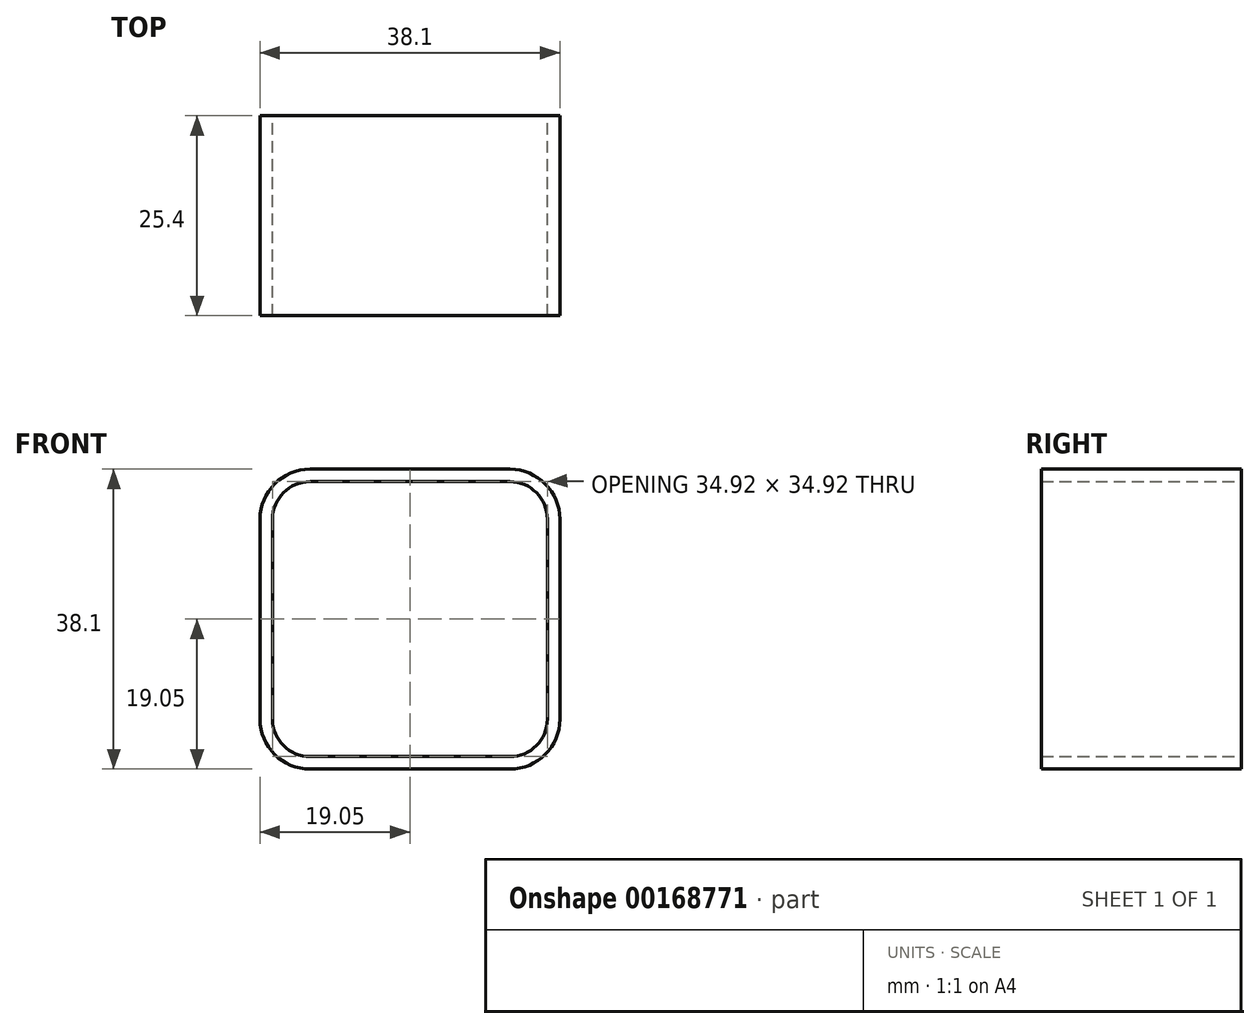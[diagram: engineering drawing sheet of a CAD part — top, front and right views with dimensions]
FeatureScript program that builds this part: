
annotation { "Feature Type Name" : "Feature", "Feature Type Description" : "" }
export const myFeature = defineFeature(function(context is Context, id is Id, definition is map)
    precondition{}
    {
        {
            var Q0;
            Q0=qCreatedBy(makeId("Front.planeOp"),FACE);
            var sketch = newSketch(context, id + "F0", { "sketchPlane" : qUnion([Q0])});
            skLineSegment(sketch, "E0.bottom", {"start": v(12.7, -19.05) * mm, "end": v(-12.7, -19.05) * mm});
            skLineSegment(sketch, "E0.top", {"start": v(12.7, 19.05) * mm, "end": v(-12.7, 19.05) * mm});
            skLineSegment(sketch, "E0.left", {"start": v(19.05, -12.7) * mm, "end": v(19.05, 12.7) * mm});
            skLineSegment(sketch, "E0.right", {"start": v(-19.05, -12.7) * mm, "end": v(-19.05, 12.7) * mm});
            skPoint(sketch, "E0.middle", {"position": v(0, 0) * mm});
            skPoint(sketch, "E1.visualSharp", {"position": v(-19.05, 19.05) * mm});
            skArc(sketch, "E1.filletArc", {"start": v(-12.7, 19.05) * mm, "mid": v(-17.2, 17.2) * mm, "end": v(-19.05, 12.7) * mm});
            skPoint(sketch, "E2.visualSharp", {"position": v(19.05, 19.05) * mm});
            skArc(sketch, "E2.filletArc", {"start": v(19.05, 12.7) * mm, "mid": v(17.2, 17.2) * mm, "end": v(12.7, 19.05) * mm});
            skPoint(sketch, "E3.visualSharp", {"position": v(19.05, -19.05) * mm});
            skArc(sketch, "E3.filletArc", {"start": v(12.7, -19.05) * mm, "mid": v(17.2, -17.2) * mm, "end": v(19.05, -12.7) * mm});
            skPoint(sketch, "E4.visualSharp", {"position": v(-19.05, -19.05) * mm});
            skArc(sketch, "E4.filletArc", {"start": v(-19.05, -12.7) * mm, "mid": v(-17.2, -17.2) * mm, "end": v(-12.7, -19.05) * mm});
            skLineSegment(sketch, "E5.0", {"start": v(12.7, 17.46) * mm, "end": v(-12.7, 17.46) * mm});
            skArc(sketch, "E5.1", {"start": v(17.46, 12.7) * mm, "mid": v(16.07, 16.07) * mm, "end": v(12.7, 17.46) * mm});
            skArc(sketch, "E5.2", {"start": v(-12.7, 17.46) * mm, "mid": v(-16.07, 16.07) * mm, "end": v(-17.46, 12.7) * mm});
            skLineSegment(sketch, "E5.3", {"start": v(17.46, -12.7) * mm, "end": v(17.46, 12.7) * mm});
            skLineSegment(sketch, "E5.4", {"start": v(-17.46, -12.7) * mm, "end": v(-17.46, 12.7) * mm});
            skArc(sketch, "E5.5", {"start": v(-17.46, -12.7) * mm, "mid": v(-16.07, -16.07) * mm, "end": v(-12.7, -17.46) * mm});
            skLineSegment(sketch, "E5.6", {"start": v(12.7, -17.46) * mm, "end": v(-12.7, -17.46) * mm});
            skArc(sketch, "E5.7", {"start": v(12.7, -17.46) * mm, "mid": v(16.07, -16.07) * mm, "end": v(17.46, -12.7) * mm});
            skSolve(sketch);
        }
        {
            var Q0;
            Q0=makeQuery(id+"F0.imprint","IMPRINT",FACE,{"disambiguationData":[TD([[makeQuery(id+"F0.imprint","IMPRINT",EDGE,{"derivedFrom":sQuery(id+"F0.wireOp",EDGE,"E0.bottom")}),-1.0]])]});
            extrude(context, id + "F1", {"entities" : qUnion([Q0]), "depth" : 25.4 * mm});
        }
    });
